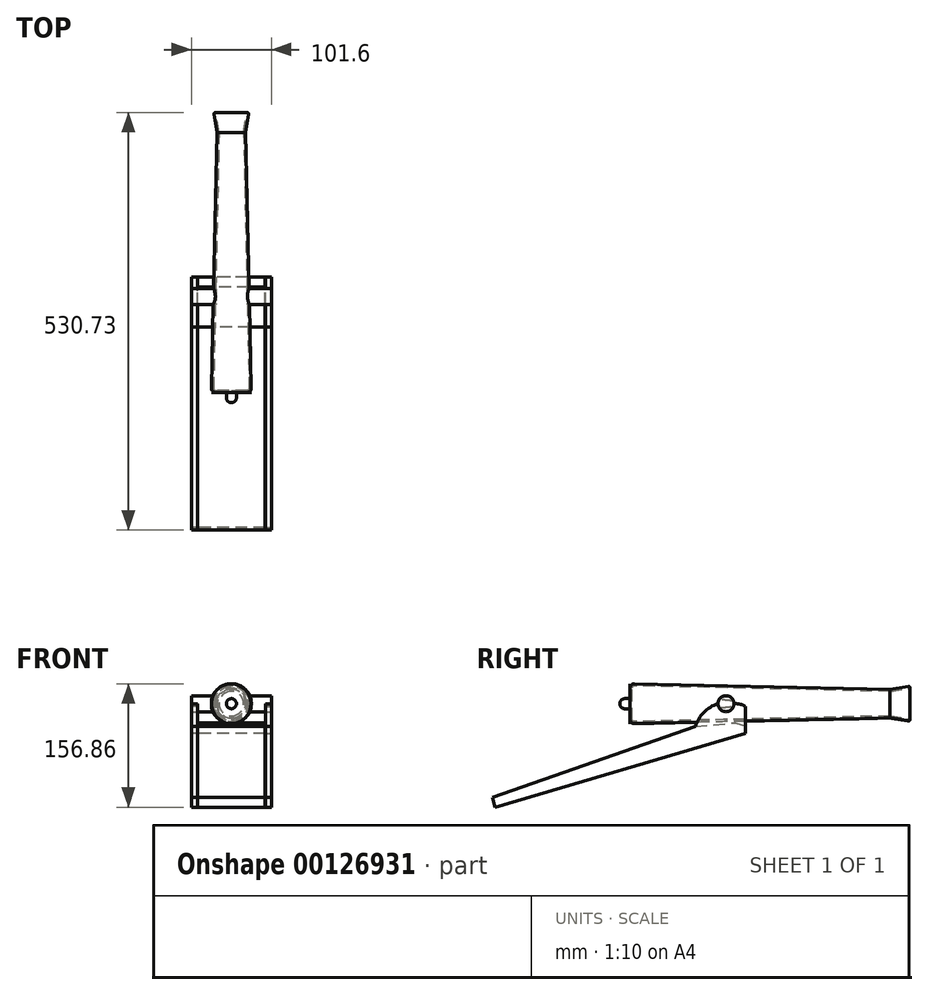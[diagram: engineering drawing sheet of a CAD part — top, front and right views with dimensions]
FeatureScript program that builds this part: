
annotation { "Feature Type Name" : "Feature", "Feature Type Description" : "" }
export const myFeature = defineFeature(function(context is Context, id is Id, definition is map)
    precondition{}
    {
        {
            var Q0;
            Q0=qCreatedBy(makeId("Front.planeOp"),FACE);
            var sketch = newSketch(context, id + "F0", { "sketchPlane" : qUnion([Q0])});
            skCircle(sketch, "E0", {"center": v(0, 0) * mm, "radius": 25.4 * mm});
            skSolve(sketch);
        }
        {
            var Q0;
            Q0 = qSketchRegion(id + "F0", true);
            extrude(context, id + "F1", {"entities" : qUnion([Q0]), "oppositeDirection" : true, "depth" : 355.6 * mm});
        }
        {
            var Q0;
            Q0=qCreatedBy(makeId("Right.planeOp"),FACE);
            var sketch = newSketch(context, id + "F2", { "sketchPlane" : qUnion([Q0])});
            skLineSegment(sketch, "E1", {"start": v(0, 25.4) * mm, "end": v(330.28, 18.2) * mm});
            skLineSegment(sketch, "E2.MirrorCS", {"start": v(0, -25.4) * mm, "end": v(330.28, -18.2) * mm});
            skLineSegment(sketch, "E3", {"start": v(330.28, 18.2) * mm, "end": v(368.17, 24.07) * mm});
            skLineSegment(sketch, "E4.MirrorCS", {"start": v(330.28, -18.2) * mm, "end": v(368.17, -24.07) * mm});
            skLineSegment(sketch, "E5", {"start": v(368.17, 24.07) * mm, "end": v(225.87, 174.87) * mm});
            skLineSegment(sketch, "E6", {"start": v(225.87, 174.87) * mm, "end": v(0, 25.4) * mm});
            skLineSegment(sketch, "E7", {"start": v(368.17, -24.07) * mm, "end": v(262.54, -154.22) * mm});
            skLineSegment(sketch, "E8", {"start": v(262.54, -154.22) * mm, "end": v(0, -25.4) * mm});
            skLineSegment(sketch, "E9", {"start": v(0, 0) * mm, "end": v(63.07, 0) * mm});
            skLineSegment(sketch, "E10", {"start": v(63.07, 0) * mm, "end": v(-45.08, 0) * mm});
            skSolve(sketch);
        }
        {
            var Q0;
            Q0=makeQuery(id+"F2.imprint","IMPRINT",FACE,{"disambiguationData":[TD([[makeQuery(id+"F2.imprint","IMPRINT",EDGE,{"derivedFrom":sQuery(id+"F2.wireOp",EDGE,"E1")}),1.0]])]});
            var Q1;
            Q1=sQuery(id+"F2.wireOp",EDGE,"E10");
            revolve(context, id + "F3", {"operationType" : NewBodyOperationType.REMOVE, "entities" : qUnion([Q0]), "axis" : qUnion([Q1]), "revolveType" : RevolveType.FULL});
        }
        {
            var Q0;
            Q0=makeQuery(id+"F3.boolean.opBoolean","INTERSECT",EDGE,{"derivedFrom":[makeQuery(id+"F1.opExtrude","CAP_FACE",FACE,{"disambiguationData":[OSD([sQuery(id+"F0.wireOp",EDGE,"E0")])],"isStart":false}),makeQuery(id+"F3.opRevolve","SWEPT_FACE",FACE,{"disambiguationData":[OSD([sQuery(id+"F2.wireOp",EDGE,"E3")])]})]});
            fillet(context, id + "F4", {"entities" : qUnion([Q0]), "radius" : 1.6 * mm, "tangentPropagation" : true, "allowEdgeOverflow" : false});
        }
        {
            var Q0;
            {var subQ0=sQuery(id+"F2.wireOp",EDGE,"E1");Q0=makeQuery(id+"F3.boolean.opBoolean","COPY",EDGE,{"disambiguationData":[TD([makeQuery(id+"F3.opRevolve","SWEPT_FACE",FACE,{"disambiguationData":[OSD([subQ0])]})])],"derivedFrom":makeQuery(id+"F3.opRevolve","SWEPT_EDGE",EDGE,{"disambiguationData":[OSD([subQ0,sQuery(id+"F2.wireOp",EDGE,"E6")])]})});}
            fillet(context, id + "F5", {"entities" : qUnion([Q0]), "radius" : 5.08 * mm, "tangentPropagation" : true, "allowEdgeOverflow" : false});
        }
        {
            var Q0;
            Q0=makeQuery(id+"F1.opExtrude","CAP_FACE",FACE,{"disambiguationData":[OSD([sQuery(id+"F0.wireOp",EDGE,"E0")])],"isStart":false});
            shell(context, id + "F6", {"entities" : qUnion([Q0]), "thickness" : 2.54 * mm});
        }
        {
            var Q0;
            Q0=makeQuery(id+"F3.boolean.opBoolean","SPLIT",FACE,{"disambiguationData":[TD([makeQuery(id+"F3.opRevolve","SWEPT_FACE",FACE,{"disambiguationData":[OSD([sQuery(id+"F2.wireOp",EDGE,"E1")])]})])],"derivedFrom":makeQuery(id+"F1.opExtrude","CAP_FACE",FACE,{"disambiguationData":[OSD([sQuery(id+"F0.wireOp",EDGE,"E0")])],"isStart":true})});
            var sketch = newSketch(context, id + "F7", { "sketchPlane" : qUnion([Q0])});
            skCircle(sketch, "E11", {"center": v(0, 0) * mm, "radius": 6.42 * mm});
            skSolve(sketch);
        }
        {
            var Q0;
            Q0 = qSketchRegion(id + "F7", true);
            extrude(context, id + "F8", {"entities" : qUnion([Q0]), "operationType" : NewBodyOperationType.ADD, "depth" : 13.04 * mm});
        }
        {
            var Q0;
            Q0=makeQuery(id+"F8.opExtrude","CAP_EDGE",EDGE,{"disambiguationData":[OSD([sQuery(id+"F7.wireOp",EDGE,"E11")])],"isStart":false});
            fillet(context, id + "F9", {"entities" : qUnion([Q0]), "radius" : 6.2 * mm, "tangentPropagation" : true, "allowEdgeOverflow" : false});
        }
        {
            var Q0;
            Q0=qCreatedBy(makeId("Right.planeOp"),FACE);
            var sketch = newSketch(context, id + "F10", { "sketchPlane" : qUnion([Q0])});
            skCircle(sketch, "E12", {"center": v(121.75, 0) * mm, "radius": 10.16 * mm});
            skSolve(sketch);
        }
        {
            var Q0;
            Q0 = qSketchRegion(id + "F10", true);
            extrude(context, id + "F11", {"entities" : qUnion([Q0]), "depth" : 50.8 * mm, "hasSecondDirection" : true, "secondDirectionOppositeDirection" : false, "secondDirectionDepth" : 19.72 * mm});
        }
        {
            var Q0;
            Q0=makeQuery(id+"F11.opExtrude","SWEPT_BODY",BODY,{"disambiguationData":[OSD([sQuery(id+"F10.wireOp",EDGE,"E12")])]});
            var Q1;
            Q1=qCreatedBy(makeId("Right.planeOp"),FACE);
            mirror(context, id + "F12", {"operationType" : NewBodyOperationType.ADD, "entities" : qUnion([Q0]), "mirrorPlane" : qUnion([Q1])});
        }
        {
            var Q0;
            Q0=makeQuery(id+"F12.opPattern","COPY",FACE,{"derivedFrom":makeQuery(id+"F11.opExtrude","CAP_FACE",FACE,{"disambiguationData":[OSD([sQuery(id+"F10.wireOp",EDGE,"E12")])],"isStart":false}),"instanceName":"1"});
            var sketch = newSketch(context, id + "F13", { "sketchPlane" : qUnion([Q0])});
            skArc(sketch, "E13", {"start": v(-131.9, 0) * mm, "mid": v(-121.75, -10.16) * mm, "end": v(-111.59, 0) * mm});
            skArc(sketch, "E14", {"start": v(-131.9, 0) * mm, "mid": v(-139.62, -0.69) * mm, "end": v(-146.71, -3.77) * mm});
            skLineSegment(sketch, "E15", {"start": v(-146.71, -3.77) * mm, "end": v(-146.71, -37.79) * mm});
            skLineSegment(sketch, "E16", {"start": v(-146.71, -37.79) * mm, "end": v(171.5, -131.46) * mm});
            skLineSegment(sketch, "E17", {"start": v(171.5, -131.46) * mm, "end": v(175.13, -119.12) * mm});
            skLineSegment(sketch, "E18", {"start": v(175.13, -119.12) * mm, "end": v(-82.74, -29) * mm});
            skArc(sketch, "E19", {"start": v(-82.74, -29) * mm, "mid": v(-93.65, -11.01) * mm, "end": v(-111.59, 0) * mm});
            skLineSegment(sketch, "E20", {"start": v(-82.74, -29) * mm, "end": v(-133.64, -24.16) * mm});
            skLineSegment(sketch, "E21", {"start": v(-133.64, -24.16) * mm, "end": v(-146.71, -28.18) * mm});
            skSolve(sketch);
        }
        {
            var Q0;
            Q0 = qSketchRegion(id + "F13", true);
            extrude(context, id + "F14", {"entities" : qUnion([Q0]), "oppositeDirection" : true, "depth" : 7.65 * mm});
        }
        {
            var Q0;
            Q0=makeQuery(id+"F14.opExtrude","SWEPT_BODY",BODY,{"disambiguationData":[OSD([sQuery(id+"F13.wireOp",EDGE,"E13"),sQuery(id+"F13.wireOp",EDGE,"E14"),sQuery(id+"F13.wireOp",EDGE,"E15"),sQuery(id+"F13.wireOp",EDGE,"E16"),sQuery(id+"F13.wireOp",EDGE,"E17"),sQuery(id+"F13.wireOp",EDGE,"E18"),sQuery(id+"F13.wireOp",EDGE,"E19")])]});
            var Q1;
            Q1=qCreatedBy(makeId("Right.planeOp"),FACE);
            mirror(context, id + "F15", {"entities" : qUnion([Q0]), "mirrorPlane" : qUnion([Q1])});
        }
        {
            var Q0;
            {var subQ0=sQuery(id+"F13.wireOp",EDGE,"E16");Q0=makeQuery(id+"F13.imprint","IMPRINT",FACE,{"disambiguationData":[TD([[makeQuery(id+"F13.imprint","IMPRINT",EDGE,{"derivedFrom":subQ0}),1.0]])]});}
            extrude(context, id + "F16", {"entities" : qUnion([Q0]), "oppositeDirection" : true, "depth" : 93.82 * mm, "hasSecondDirection" : true, "secondDirectionOppositeDirection" : true, "secondDirectionDepth" : 7.6 * mm});
        }
    });
